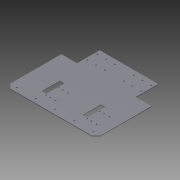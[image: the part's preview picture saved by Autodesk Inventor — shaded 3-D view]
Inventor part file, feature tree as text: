
AUTODESK INVENTOR PART (.ipt)
format: ipt  version: 2014 (Build 180170000, 170)  size: 209,408 bytes
history: native  units: mm
features: sketch x19, other x5, hole x4, chamfer x1
ambient origin geometry x8: Origin, YZ Plane, XZ Plane, XY Plane, X Axis, Y Axis, Z Axis, Center Point
bodies: Body1 (feature_tree)
feature tree (29):
  other  "Sólido1"
  other  "Cara1"
  chamfer  "Chaflán de esquina1"  Distance=10.0mm Angle=45.0deg
  hole  "Agujero16"  [1 undecoded]
  hole  "Hole17"  [1 undecoded]
  hole  "Hole18"  [1 undecoded]
  sketch  "Boceto1"  dims[d0=200.0mm]
  other  "Placa1"
  sketch  "Boceto2"  dims[d1=173.0mm]
  sketch  "Boceto5"  dims[d2=100.0mm]
  sketch  "Boceto6"  dims[d4=1.5mm]
  sketch  "Boceto7"  dims[d6=50.0mm]
  sketch  "Boceto8"  dims[d9=50.0mm]
  sketch  "Boceto9"  dims[d52=35.0mm]
  sketch  "Boceto10"  dims[d58=35.0mm]
  sketch  "Boceto11"  dims[d59=1.5mm]
  sketch  "Boceto12"  dims[d60=0.0mm d124=10.0mm d125=6.0mm d126=45.0deg]
  sketch  "Boceto13"  dims[d127=105.0mm]
  sketch  "Boceto14"  dims[d128=3.2mm d129=6.0mm d130=4.0mm d131=2.0mm d132=90.0deg d133=8.0mm d134=0.0mm d149=1.5mm]
  sketch  "Boceto15"  dims[d150=0.0mm d151=3.0mm]
  sketch  "Boceto16"  dims[d152=3.0mm d153=3.0mm d154=3.0mm]
  sketch  "Boceto17"  dims[d155=3.0mm d156=3.0mm]
  sketch  "Boceto18"  dims[d164=3.0mm d165=6.0mm d166=4.0mm d167=2.0mm d168=90.0deg d169=1.5mm d170=20.594885mm]
  hole  "Hole16"  [1 undecoded]
  sketch  "Boceto20"  dims[d171=10.0mm]
  sketch  "Boceto21"  dims[d172=40.0mm]
  sketch  "Boceto22"  dims[d175=3.0mm d176=3.0mm d177=3.0mm d178=3.0mm d179=3.0mm d180=6.0mm d181=4.0mm d182=2.0mm d183=90.0deg d184=1.5mm d185=20.594885mm d186=3.0mm d187=3.0mm d188=3.0mm d189=3.0mm d190=40.671134mm d191=40.671134mm d192=40.0mm d193=10.0mm d194=11.886709mm d195=8.926654mm d196=2.492184mm d197=8.926654mm d198=11.886709mm d200=28.341534mm d201=8.926654mm d202=11.886709mm d203=8.926654mm d204=11.886709mm d205=28.341534mm d207=2.492184mm]
  other  "Cortar3"
  other  "Cortar6"
note: 4 required parameter values undecoded (feature->parameter linkage not recoverable at this tier; creation-order binding heuristic only, values carry confidence <= 0.55)
